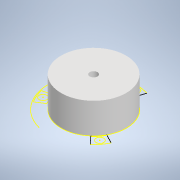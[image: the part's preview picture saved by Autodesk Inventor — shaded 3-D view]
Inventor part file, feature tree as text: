
AUTODESK INVENTOR PART (.ipt)
format: ipt  version: 2022 (Build 260153000, 153)  size: 190,464 bytes
history: native  units: in
note: dims shown in document units (in); Inventor stores cm internally (conversion verified against a paired STEP export)
features: extrude x4, sketch x4, projected_geometry x3, fillet x1
ambient origin geometry x8: Origin, YZ Plane, XZ Plane, XY Plane, X Axis, Y Axis, Z Axis, Center Point
bodies: Solid1 (feature_tree)
feature tree (12):
  extrude  "Extrusion1"  Depth=0.1181in
  extrude  "Extrusion3"  Depth=0.1181in
  extrude  "Extrusion4"  Depth=0.0591in
  extrude  "Extrusion5"  Depth=0.05in
  fillet  "Fillet1"  Radius=0.15in
  sketch  "Sketch1"  dims[d0=0.1181in d1=1.0in]
  sketch  "Sketch3"  dims[d2=0.1181in d3=0.0in d14=0.875in]
  sketch  "Sketch4"  dims[d15=0.3487in d16=0.0in d17=0.0591in]
  projected_geometry  "Projected Loop2"
  projected_geometry  "Projected Loop3"
  sketch  "Sketch5"  dims[d18=0.3in d19=0.05in d20=0.15in d21=0.05in d22=0.15in d23=0.0787in d24=0.0in d28=0.075in d29=45.0deg d30=135.0deg d31=7.874in d33=360.0deg d35=0.0787in d36=0.0in d37=0.275in d38=0.05in d39=0.15in d40=0.05in d41=135.0deg d42=0.05in]
  projected_geometry  "Projected Loop4"
